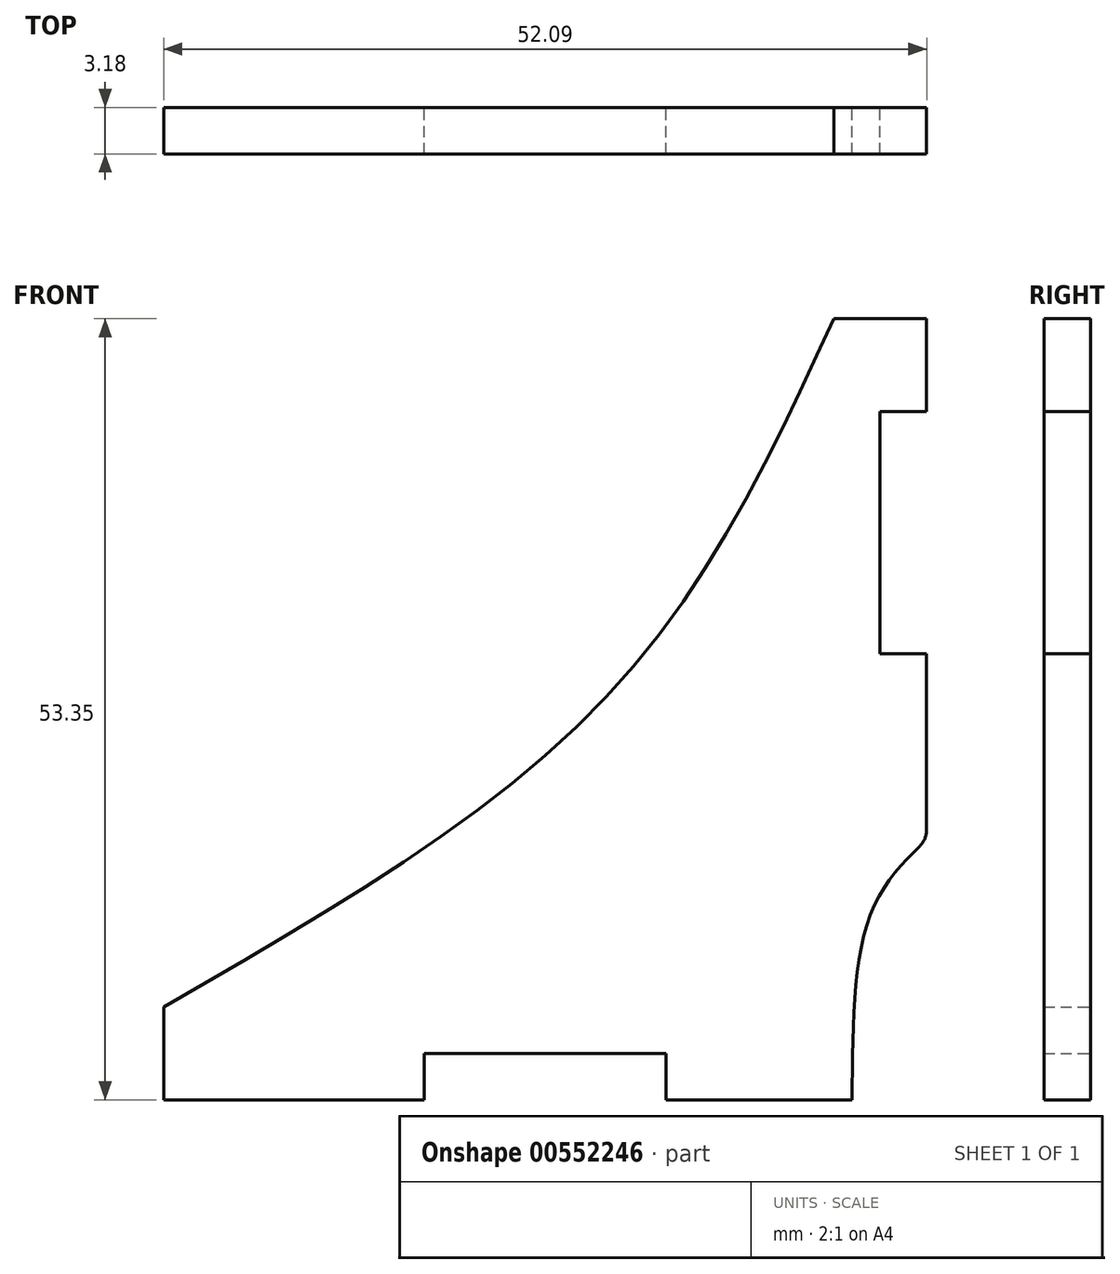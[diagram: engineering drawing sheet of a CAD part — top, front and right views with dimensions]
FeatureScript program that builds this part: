
annotation { "Feature Type Name" : "Feature", "Feature Type Description" : "" }
export const myFeature = defineFeature(function(context is Context, id is Id, definition is map)
    precondition{}
    {
        {
            var Q0;
            Q0=qCreatedBy(makeId("Front.planeOp"),FACE);
            var sketch = newSketch(context, id + "F0", { "sketchPlane" : qUnion([Q0])});
            skLineSegment(sketch, "E0", {"start": v(-8.26, 0) * mm, "end": v(-26.05, 0) * mm});
            skLineSegment(sketch, "E1", {"start": v(8.26, 0) * mm, "end": v(20.96, 0) * mm});
            skFitSpline(sketch, "E2", {"points": [v(20.96, 0) * mm, v(22.22, 12.7) * mm, v(26.04, 17.78) * mm], "startDerivative": vector(0.1, 24.4) * mm, "endDerivative": vector(10.67, 10.34) * mm});
            skLineSegment(sketch, "E3", {"start": v(26.04, 18.43) * mm, "end": v(26.04, 30.48) * mm});
            skLineSegment(sketch, "E4", {"start": v(-26.05, 0) * mm, "end": v(-26.05, 6.35) * mm});
            skLineSegment(sketch, "E5", {"start": v(26.04, 47) * mm, "end": v(26.04, 53.35) * mm});
            skArc(sketch, "E6.filletArc", {"start": v(25.57, 17.33) * mm, "mid": v(25.91, 17.83) * mm, "end": v(26.04, 18.43) * mm});
            skFitSpline(sketch, "E7", {"points": [v(-26.05, 6.35) * mm, v(4.45, 27.82) * mm, v(19.7, 53.35) * mm], "startDerivative": vector(64.44, 37.07) * mm, "endDerivative": vector(26.32, 57.3) * mm});
            skLineSegment(sketch, "E8", {"start": v(19.7, 53.35) * mm, "end": v(26.04, 53.35) * mm});
            skLineSegment(sketch, "E9", {"start": v(-8.26, 3.18) * mm, "end": v(8.26, 3.17) * mm});
            skLineSegment(sketch, "E10", {"start": v(22.86, 30.48) * mm, "end": v(22.86, 47) * mm});
            skLineSegment(sketch, "E11", {"start": v(22.86, 47) * mm, "end": v(26.04, 47) * mm});
            skLineSegment(sketch, "E12", {"start": v(22.86, 30.48) * mm, "end": v(26.04, 30.48) * mm});
            skLineSegment(sketch, "E13", {"start": v(-8.26, 0) * mm, "end": v(-8.26, 3.18) * mm});
            skLineSegment(sketch, "E14", {"start": v(8.26, 0) * mm, "end": v(8.26, 3.17) * mm});
            skSolve(sketch);
        }
        {
            var Q0;
            Q0 = qSketchRegion(id + "F0", true);
            extrude(context, id + "F1", {"entities" : qUnion([Q0]), "depth" : 3.17 * mm, "offsetDistance" : 25.4 * mm});
        }
    });
